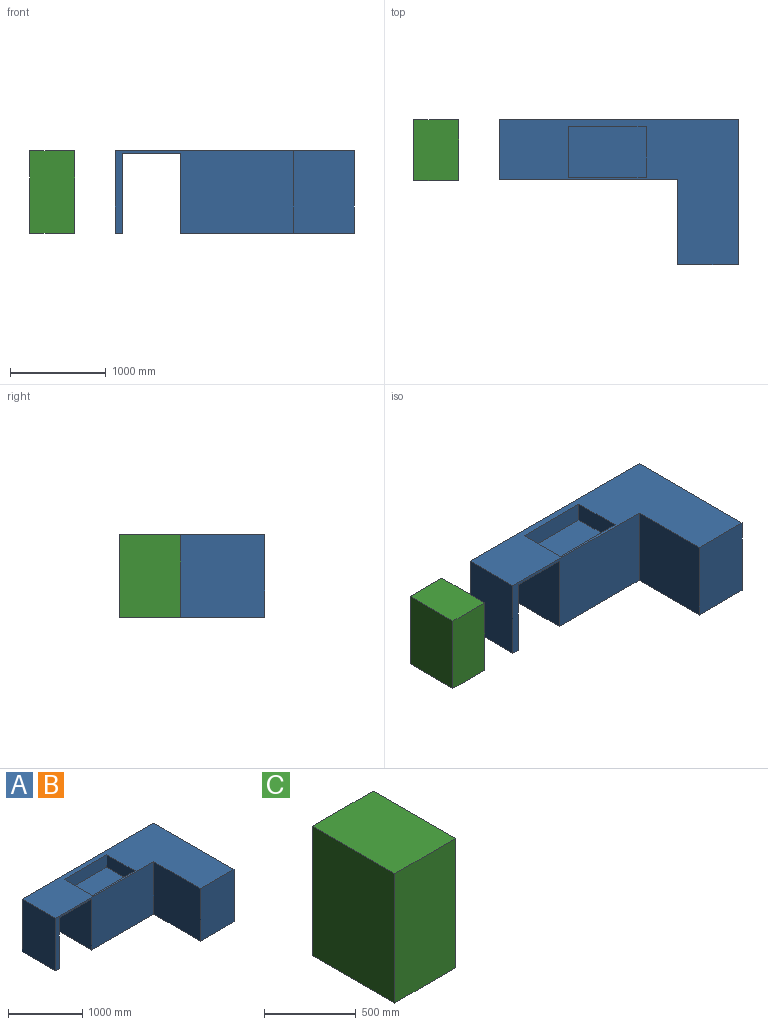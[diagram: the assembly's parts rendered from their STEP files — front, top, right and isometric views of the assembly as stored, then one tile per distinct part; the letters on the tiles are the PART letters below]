
ASSEMBLY  parts=3 mates=1
PART A: 17 faces, bbox 2501.9x1524x863.6 mm
  f0: plane 1816.1x1524mm, normal (0,0,-1), area 1717738.5mm2, adj f2,f3,f4,f5,f6,f11
  f1: plane 863.6x635mm, normal (-1,0,0), area 548386mm2, adj f2,f6,f7,f8
  f2: plane 1866.9x863.6mm, normal (0,-1,0), area 1101288.1mm2, adj f0,f1,f3,f7,f8,f9,f10,f11
  f3: plane 889x863.6mm, normal (-1,0,0), area 767740.4mm2, adj f0,f2,f4,f8
  f4: plane 863.6x635mm, normal (0,-1,0), area 548386mm2, adj f0,f3,f5,f8
  f5: plane 1524x863.6mm, normal (1,0,0), area 1316126.4mm2, adj f0,f4,f6,f8
  f6: plane 2501.9x863.6mm, normal (0,1,0), area 1649674.1mm2, adj f0,f1,f5,f7,f8,f9,f10,f11
  f7: plane 635x76.2mm, normal (0,0,-1), area 48387mm2, adj f1,f2,f6,f10
  f8: plane 2501.9x1524mm, normal (0,0,1), area 1719674mm2, adj f1,f2,f3,f4,f5,f6,f12,f13
  f9: plane 635x609.6mm, normal (0,0,-1), area 387096mm2, adj f2,f6,f10,f11
  f10: plane 838.2x635mm, normal (1,0,0), area 532257mm2, adj f2,f6,f7,f9
  f11: plane 838.2x635mm, normal (-1,0,0), area 532257mm2, adj f0,f2,f6,f9
  f12: plane 812.8x203.2mm, normal (0,1,0), area 165161mm2, adj f8,f13,f15,f16
  f13: plane 533.4x203.2mm, normal (-1,0,0), area 108386.9mm2, adj f8,f12,f14,f16
  f14: plane 812.8x203.2mm, normal (0,-1,0), area 165161mm2, adj f8,f13,f15,f16
  f15: plane 533.4x203.2mm, normal (1,0,0), area 108386.9mm2, adj f8,f12,f14,f16
  f16: plane 812.8x533.4mm, normal (0,0,1), area 433547.5mm2, adj f12,f13,f14,f15
PART B: same geometry as A
PART C: 6 faces, bbox 469.9x635x863.6 mm
  f0: plane 863.6x469.9mm, normal (0,1,0), area 405805.6mm2, adj f1,f3,f4,f5
  f1: plane 863.6x635mm, normal (-1,0,0), area 548386mm2, adj f0,f2,f4,f5
  f2: plane 863.6x469.9mm, normal (0,-1,0), area 405805.6mm2, adj f1,f3,f4,f5
  f3: plane 863.6x635mm, normal (1,0,0), area 548386mm2, adj f0,f2,f4,f5
  f4: plane 635x469.9mm, normal (0,0,-1), area 298386.5mm2, adj f0,f1,f2,f3
  f5: plane 635x469.9mm, normal (0,0,1), area 298386.5mm2, adj f0,f1,f2,f3
PLACE A t=(-99.73,8.51,-135.81)mm
PLACE B t=(-99.73,8.51,-135.81)mm
PLACE C t=(-2011.02,1.65,-137.74)mm
MATE parallel C.f3 <-> A.f1  axis (1,0,0) through (-1776.07,1.65,-569.54)mm
